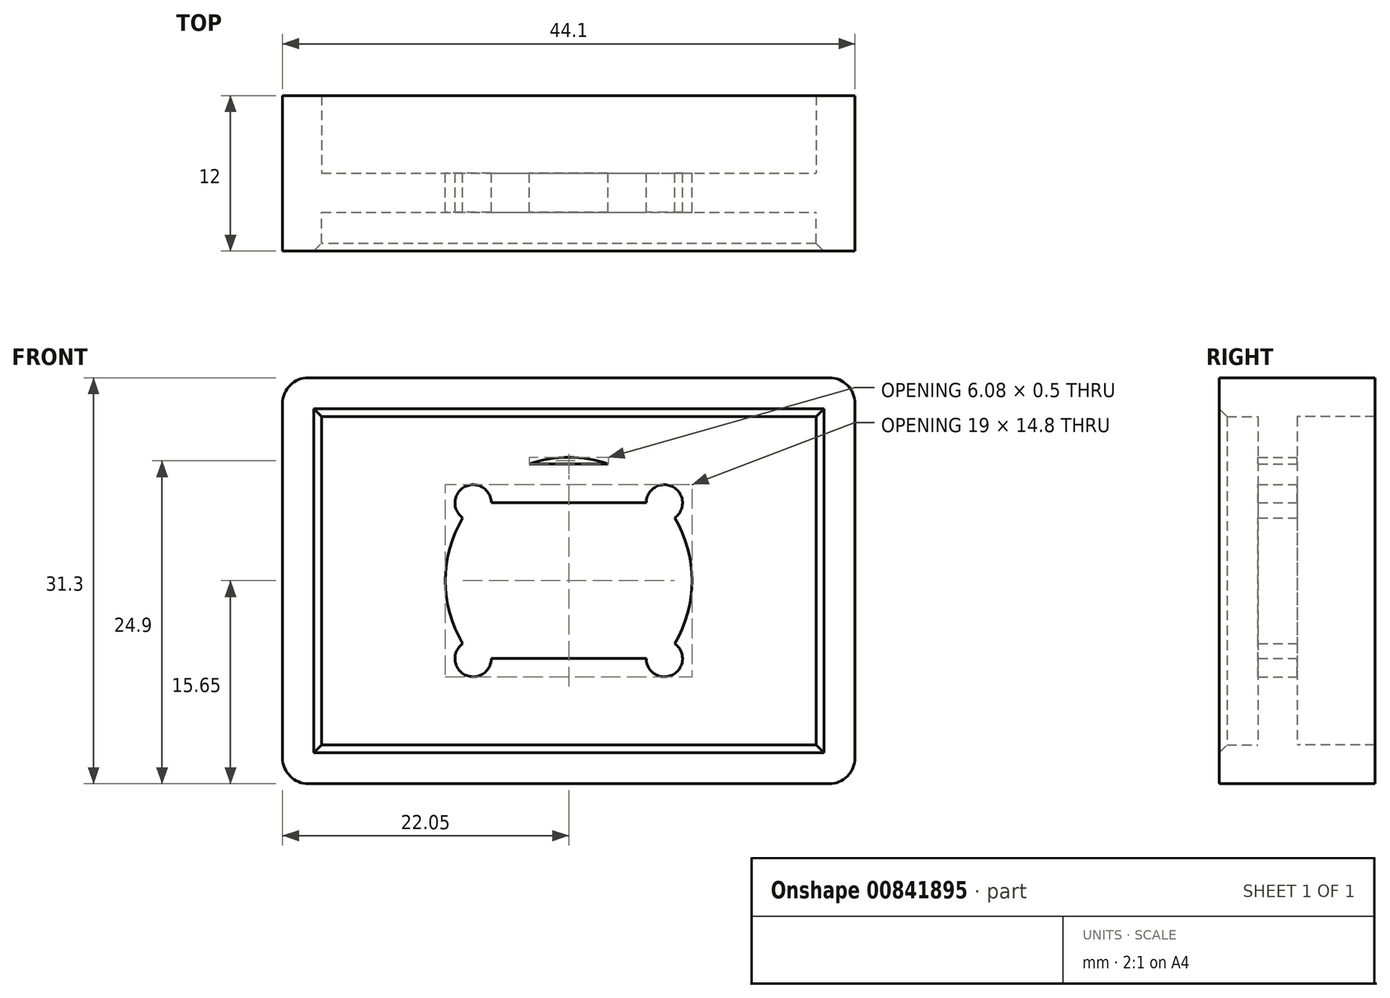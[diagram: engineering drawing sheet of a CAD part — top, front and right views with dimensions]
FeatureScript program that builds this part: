
annotation { "Feature Type Name" : "Feature", "Feature Type Description" : "" }
export const myFeature = defineFeature(function(context is Context, id is Id, definition is map)
    precondition{}
    {
        {
            var Q0;
            Q0=qCreatedBy(makeId("Front.planeOp"),FACE);
            var sketch = newSketch(context, id + "F0", { "sketchPlane" : qUnion([Q0])});
            skLineSegment(sketch, "E0.bottom", {"start": v(-19.05, 12.65) * mm, "end": v(19.05, 12.65) * mm});
            skLineSegment(sketch, "E0.top", {"start": v(-19.05, -12.65) * mm, "end": v(19.05, -12.65) * mm});
            skLineSegment(sketch, "E0.left", {"start": v(-19.05, 12.65) * mm, "end": v(-19.05, -12.65) * mm});
            skLineSegment(sketch, "E0.right", {"start": v(19.05, 12.65) * mm, "end": v(19.05, -12.65) * mm});
            skPoint(sketch, "E0.middle", {"position": v(0, 0) * mm});
            skLineSegment(sketch, "E1.bottom", {"start": v(-22.05, 15.65) * mm, "end": v(22.05, 15.65) * mm});
            skLineSegment(sketch, "E1.top", {"start": v(-22.05, -15.65) * mm, "end": v(22.05, -15.65) * mm});
            skLineSegment(sketch, "E1.left", {"start": v(-22.05, 15.65) * mm, "end": v(-22.05, -15.65) * mm});
            skLineSegment(sketch, "E1.right", {"start": v(22.05, 15.65) * mm, "end": v(22.05, -15.65) * mm});
            skCircle(sketch, "E2", {"center": v(0, 0) * mm, "radius": 9.5 * mm});
            skLineSegment(sketch, "E3.bottom", {"start": v(-9.5, 6) * mm, "end": v(9.5, 6) * mm});
            skLineSegment(sketch, "E3.top", {"start": v(-9.5, -6) * mm, "end": v(9.5, -6) * mm});
            skLineSegment(sketch, "E3.left", {"start": v(-9.5, 6) * mm, "end": v(-9.5, -6) * mm});
            skLineSegment(sketch, "E3.right", {"start": v(9.5, 6) * mm, "end": v(9.5, -6) * mm});
            skCircle(sketch, "E4", {"center": v(0, 0) * mm, "radius": 12.5 * mm});
            skLineSegment(sketch, "E5.bottom", {"start": v(-12.5, 9) * mm, "end": v(12.5, 9) * mm});
            skLineSegment(sketch, "E5.top", {"start": v(-12.5, -9) * mm, "end": v(12.5, -9) * mm});
            skLineSegment(sketch, "E5.left", {"start": v(-12.5, 9) * mm, "end": v(-12.5, -9) * mm});
            skLineSegment(sketch, "E5.right", {"start": v(12.5, 9) * mm, "end": v(12.5, -9) * mm});
            skLineSegment(sketch, "E6.bottom", {"start": v(-7.37, 6) * mm, "end": v(7.37, 6) * mm});
            skLineSegment(sketch, "E6.top", {"start": v(-7.37, -6) * mm, "end": v(7.37, -6) * mm});
            skLineSegment(sketch, "E6.left", {"start": v(-7.37, 6) * mm, "end": v(-7.37, -6) * mm});
            skLineSegment(sketch, "E6.right", {"start": v(7.37, 6) * mm, "end": v(7.37, -6) * mm});
            skCircle(sketch, "E7", {"center": v(-7.37, 6) * mm, "radius": 1.4 * mm});
            skCircle(sketch, "E8", {"center": v(7.37, 6) * mm, "radius": 1.4 * mm});
            skCircle(sketch, "E9", {"center": v(7.37, -6) * mm, "radius": 1.4 * mm});
            skCircle(sketch, "E10", {"center": v(-7.37, -6) * mm, "radius": 1.4 * mm});
            skSolve(sketch);
        }
        {
            var Q0;
            {var subQ0=sQuery(id+"F0.wireOp",EDGE,"diyo5Ijy-Unrl-Ix7s-xjxT-a2Idyrmd7R7O");var subQ1=sQuery(id+"F0.wireOp",EDGE,"E4");var subQ2=makeQuery(id+"F0.imprint","INTERSECT",VERTEX,{"disambiguationData":[OD(0.0)],"derivedFrom":[subQ1,subQ0]});Q0=makeQuery(id+"F0.imprint","IMPRINT",FACE,{"disambiguationData":[TD([[makeQuery(id+"F0.imprint","IMPRINT",EDGE,{"disambiguationData":[TD([[subQ2,-1.0]])],"derivedFrom":subQ1}),1.0]])]});}
            var Q1;
            {var subQ0=sQuery(id+"F0.wireOp",EDGE,"5QQwORZ6-yYhv-RJ5g-prPR-Qrd3KqkXHQQd");var subQ1=sQuery(id+"F0.wireOp",EDGE,"E4");var subQ2=makeQuery(id+"F0.imprint","INTERSECT",VERTEX,{"disambiguationData":[OD(0.0)],"derivedFrom":[subQ1,subQ0]});Q1=makeQuery(id+"F0.imprint","IMPRINT",FACE,{"disambiguationData":[TD([[makeQuery(id+"F0.imprint","IMPRINT",EDGE,{"disambiguationData":[TD([[subQ2,-1.0]])],"derivedFrom":subQ1}),1.0]])]});}
            var Q2;
            Q2=makeQuery(id+"F0.imprint","IMPRINT",FACE,{"disambiguationData":[TD([[makeQuery(id+"F0.imprint","IMPRINT",EDGE,{"derivedFrom":sQuery(id+"F0.wireOp",EDGE,"E0.bottom")}),-1.0]])]});
            var Q3;
            {var subQ0=sQuery(id+"F0.wireOp",EDGE,"E5.bottom");var subQ1=sQuery(id+"F0.wireOp",EDGE,"E2");var subQ2=makeQuery(id+"F0.imprint","INTERSECT",VERTEX,{"disambiguationData":[OD(0.0)],"derivedFrom":[subQ1,subQ0]});Q3=makeQuery(id+"F0.imprint","IMPRINT",FACE,{"disambiguationData":[TD([[makeQuery(id+"F0.imprint","IMPRINT",EDGE,{"disambiguationData":[TD([[subQ2,-1.0]])],"derivedFrom":subQ1}),-1.0]])]});}
            var Q4;
            {var subQ0=sQuery(id+"F0.wireOp",EDGE,"RQsxDqyy-hhwE-D28E-GqSd-PO1LcPHCWcnN");var subQ1=sQuery(id+"F0.wireOp",EDGE,"E4");var subQ2=makeQuery(id+"F0.imprint","INTERSECT",VERTEX,{"disambiguationData":[OD(0.0)],"derivedFrom":[subQ1,subQ0]});Q4=makeQuery(id+"F0.imprint","IMPRINT",FACE,{"disambiguationData":[TD([[makeQuery(id+"F0.imprint","IMPRINT",EDGE,{"disambiguationData":[TD([[subQ2,-1.0]])],"derivedFrom":subQ1}),-1.0]])]});}
            var Q5;
            {var subQ0=sQuery(id+"F0.wireOp",EDGE,"E5.right");var subQ1=sQuery(id+"F0.wireOp",EDGE,"E4");var subQ2=makeQuery(id+"F0.imprint","INTERSECT",VERTEX,{"derivedFrom":[subQ1,subQ0]});Q5=makeQuery(id+"F0.imprint","IMPRINT",FACE,{"disambiguationData":[TD([[makeQuery(id+"F0.imprint","IMPRINT",EDGE,{"disambiguationData":[TD([[subQ2,1.0]])],"derivedFrom":subQ1}),-1.0]])]});}
            var Q6;
            {var subQ0=sQuery(id+"F0.wireOp",EDGE,"E5.top");var subQ1=sQuery(id+"F0.wireOp",EDGE,"E2");var subQ5=makeQuery(id+"F0.imprint","INTERSECT",VERTEX,{"disambiguationData":[OD(0.0)],"derivedFrom":[subQ1,subQ0]});Q6=makeQuery(id+"F0.imprint","IMPRINT",FACE,{"disambiguationData":[TD([[makeQuery(id+"F0.imprint","IMPRINT",EDGE,{"disambiguationData":[TD([[subQ5,-1.0]])],"derivedFrom":subQ1}),-1.0]])]});}
            var Q7;
            {var subQ0=sQuery(id+"F0.wireOp",EDGE,"E5.left");var subQ1=sQuery(id+"F0.wireOp",EDGE,"E4");var subQ2=makeQuery(id+"F0.imprint","INTERSECT",VERTEX,{"derivedFrom":[subQ1,subQ0]});Q7=makeQuery(id+"F0.imprint","IMPRINT",FACE,{"disambiguationData":[TD([[makeQuery(id+"F0.imprint","IMPRINT",EDGE,{"disambiguationData":[TD([[subQ2,-1.0]])],"derivedFrom":subQ1}),-1.0]])]});}
            var Q8;
            {var subQ0=sQuery(id+"F0.wireOp",EDGE,"E5.bottom");var subQ1=sQuery(id+"F0.wireOp",EDGE,"E2");var subQ2=makeQuery(id+"F0.imprint","INTERSECT",VERTEX,{"disambiguationData":[OD(0.0)],"derivedFrom":[subQ1,subQ0]});Q8=makeQuery(id+"F0.imprint","IMPRINT",FACE,{"disambiguationData":[TD([[makeQuery(id+"F0.imprint","IMPRINT",EDGE,{"disambiguationData":[TD([[subQ2,-1.0]])],"derivedFrom":subQ1}),1.0]])]});}
            var Q9;
            {var subQ0=sQuery(id+"F0.wireOp",EDGE,"E5.top");var subQ1=sQuery(id+"F0.wireOp",EDGE,"E2");var subQ2=makeQuery(id+"F0.imprint","INTERSECT",VERTEX,{"disambiguationData":[OD(0.0)],"derivedFrom":[subQ1,subQ0]});Q9=makeQuery(id+"F0.imprint","IMPRINT",FACE,{"disambiguationData":[TD([[makeQuery(id+"F0.imprint","IMPRINT",EDGE,{"disambiguationData":[TD([[subQ2,-1.0]])],"derivedFrom":subQ1}),1.0]])]});}
            var Q10;
            {var subQ0=sQuery(id+"F0.wireOp",EDGE,"diyo5Ijy-Unrl-Ix7s-xjxT-a2Idyrmd7R7O");var subQ1=sQuery(id+"F0.wireOp",EDGE,"E4");var subQ2=makeQuery(id+"F0.imprint","INTERSECT",VERTEX,{"disambiguationData":[OD(1.0)],"derivedFrom":[subQ1,subQ0]});Q10=makeQuery(id+"F0.imprint","IMPRINT",FACE,{"disambiguationData":[TD([[makeQuery(id+"F0.imprint","IMPRINT",EDGE,{"disambiguationData":[TD([[subQ2,-1.0]])],"derivedFrom":subQ1}),-1.0]])]});}
            var Q11;
            {var subQ0=sQuery(id+"F0.wireOp",EDGE,"E5.bottom");var subQ1=sQuery(id+"F0.wireOp",EDGE,"E2");var subQ2=makeQuery(id+"F0.imprint","INTERSECT",VERTEX,{"disambiguationData":[OD(1.0)],"derivedFrom":[subQ1,subQ0]});Q11=makeQuery(id+"F0.imprint","IMPRINT",FACE,{"disambiguationData":[TD([[makeQuery(id+"F0.imprint","IMPRINT",EDGE,{"disambiguationData":[TD([[subQ2,-1.0]])],"derivedFrom":subQ1}),-1.0]])]});}
            var Q12;
            {var subQ0=sQuery(id+"F0.wireOp",EDGE,"diyo5Ijy-Unrl-Ix7s-xjxT-a2Idyrmd7R7O");var subQ1=sQuery(id+"F0.wireOp",EDGE,"E4");var subQ2=makeQuery(id+"F0.imprint","INTERSECT",VERTEX,{"disambiguationData":[OD(0.0)],"derivedFrom":[subQ1,subQ0]});Q12=makeQuery(id+"F0.imprint","IMPRINT",FACE,{"disambiguationData":[TD([[makeQuery(id+"F0.imprint","IMPRINT",EDGE,{"disambiguationData":[TD([[subQ2,-1.0]])],"derivedFrom":subQ1}),-1.0]])]});}
            var Q13;
            {var subQ0=sQuery(id+"F0.wireOp",EDGE,"RQsxDqyy-hhwE-D28E-GqSd-PO1LcPHCWcnN");var subQ1=sQuery(id+"F0.wireOp",EDGE,"E4");var subQ2=makeQuery(id+"F0.imprint","INTERSECT",VERTEX,{"disambiguationData":[OD(0.0)],"derivedFrom":[subQ1,subQ0]});Q13=makeQuery(id+"F0.imprint","IMPRINT",FACE,{"disambiguationData":[TD([[makeQuery(id+"F0.imprint","IMPRINT",EDGE,{"disambiguationData":[TD([[subQ2,1.0]])],"derivedFrom":subQ1}),-1.0]])]});}
            var Q14;
            {var subQ0=sQuery(id+"F0.wireOp",EDGE,"5QQwORZ6-yYhv-RJ5g-prPR-Qrd3KqkXHQQd");var subQ1=sQuery(id+"F0.wireOp",EDGE,"E4");var subQ2=makeQuery(id+"F0.imprint","INTERSECT",VERTEX,{"disambiguationData":[OD(0.0)],"derivedFrom":[subQ1,subQ0]});Q14=makeQuery(id+"F0.imprint","IMPRINT",FACE,{"disambiguationData":[TD([[makeQuery(id+"F0.imprint","IMPRINT",EDGE,{"disambiguationData":[TD([[subQ2,-1.0]])],"derivedFrom":subQ1}),-1.0]])]});}
            var Q15;
            {var subQ0=sQuery(id+"F0.wireOp",EDGE,"Sn6az9JK-Su7q-VoNe-VHIh-EGGie5zRdxJw");var subQ1=sQuery(id+"F0.wireOp",EDGE,"E4");var subQ2=makeQuery(id+"F0.imprint","INTERSECT",VERTEX,{"disambiguationData":[OD(0.0)],"derivedFrom":[subQ1,subQ0]});Q15=makeQuery(id+"F0.imprint","IMPRINT",FACE,{"disambiguationData":[TD([[makeQuery(id+"F0.imprint","IMPRINT",EDGE,{"disambiguationData":[TD([[subQ2,-1.0]])],"derivedFrom":subQ1}),-1.0]])]});}
            var Q16;
            {var subQ6=sQuery(id+"F0.wireOp",EDGE,"E3.left");var subQ7=makeQuery(id+"F0.imprint","INTERSECT",VERTEX,{"derivedFrom":[sQuery(id+"F0.wireOp",EDGE,"E2"),subQ6]});Q16=makeQuery(id+"F0.imprint","IMPRINT",FACE,{"disambiguationData":[TD([[makeQuery(id+"F0.imprint","IMPRINT",EDGE,{"disambiguationData":[TD([[subQ7,1.0]])],"derivedFrom":subQ6}),-1.0]])]});}
            var Q17;
            {var subQ6=sQuery(id+"F0.wireOp",EDGE,"E3.right");var subQ8=makeQuery(id+"F0.imprint","INTERSECT",VERTEX,{"derivedFrom":[sQuery(id+"F0.wireOp",EDGE,"E2"),subQ6]});Q17=makeQuery(id+"F0.imprint","IMPRINT",FACE,{"disambiguationData":[TD([[makeQuery(id+"F0.imprint","IMPRINT",EDGE,{"disambiguationData":[TD([[subQ8,1.0]])],"derivedFrom":subQ6}),1.0]])]});}
            var Q18;
            {var subQ0=sQuery(id+"F0.wireOp",EDGE,"E5.top");var subQ1=sQuery(id+"F0.wireOp",EDGE,"E2");var subQ2=makeQuery(id+"F0.imprint","INTERSECT",VERTEX,{"disambiguationData":[OD(1.0)],"derivedFrom":[subQ1,subQ0]});Q18=makeQuery(id+"F0.imprint","IMPRINT",FACE,{"disambiguationData":[TD([[makeQuery(id+"F0.imprint","IMPRINT",EDGE,{"disambiguationData":[TD([[subQ2,-1.0]])],"derivedFrom":subQ1}),-1.0]])]});}
            var Q19;
            {var subQ0=sQuery(id+"F0.wireOp",EDGE,"E3.right");var subQ1=sQuery(id+"F0.wireOp",EDGE,"E2");var subQ2=makeQuery(id+"F0.imprint","INTERSECT",VERTEX,{"derivedFrom":[subQ1,subQ0]});Q19=makeQuery(id+"F0.imprint","IMPRINT",FACE,{"disambiguationData":[TD([[makeQuery(id+"F0.imprint","IMPRINT",EDGE,{"disambiguationData":[TD([[subQ2,1.0]])],"derivedFrom":subQ1}),-1.0]])]});}
            var Q20;
            {var subQ0=sQuery(id+"F0.wireOp",EDGE,"E3.left");var subQ1=sQuery(id+"F0.wireOp",EDGE,"E2");var subQ2=makeQuery(id+"F0.imprint","INTERSECT",VERTEX,{"derivedFrom":[subQ1,subQ0]});Q20=makeQuery(id+"F0.imprint","IMPRINT",FACE,{"disambiguationData":[TD([[makeQuery(id+"F0.imprint","IMPRINT",EDGE,{"disambiguationData":[TD([[subQ2,-1.0]])],"derivedFrom":subQ1}),-1.0]])]});}
            var Q21;
            {var subQ0=sQuery(id+"F0.wireOp",EDGE,"E3.left");var subQ1=sQuery(id+"F0.wireOp",EDGE,"E3.bottom");var subQ2=makeQuery(id+"F0.imprint","INTERSECT",VERTEX,{"derivedFrom":[subQ1,subQ0]});Q21=makeQuery(id+"F0.imprint","IMPRINT",FACE,{"disambiguationData":[TD([[makeQuery(id+"F0.imprint","IMPRINT",EDGE,{"disambiguationData":[TD([[subQ2,-1.0]])],"derivedFrom":subQ1}),-1.0]])]});}
            var Q22;
            {var subQ0=sQuery(id+"F0.wireOp",EDGE,"E3.right");var subQ1=sQuery(id+"F0.wireOp",EDGE,"E3.bottom");var subQ2=makeQuery(id+"F0.imprint","INTERSECT",VERTEX,{"derivedFrom":[subQ1,subQ0]});Q22=makeQuery(id+"F0.imprint","IMPRINT",FACE,{"disambiguationData":[TD([[makeQuery(id+"F0.imprint","IMPRINT",EDGE,{"disambiguationData":[TD([[subQ2,1.0]])],"derivedFrom":subQ1}),-1.0]])]});}
            var Q23;
            {var subQ0=sQuery(id+"F0.wireOp",EDGE,"E3.left");var subQ1=sQuery(id+"F0.wireOp",EDGE,"E3.top");var subQ2=makeQuery(id+"F0.imprint","INTERSECT",VERTEX,{"derivedFrom":[subQ1,subQ0]});Q23=makeQuery(id+"F0.imprint","IMPRINT",FACE,{"disambiguationData":[TD([[makeQuery(id+"F0.imprint","IMPRINT",EDGE,{"disambiguationData":[TD([[subQ2,-1.0]])],"derivedFrom":subQ1}),1.0]])]});}
            var Q24;
            {var subQ0=sQuery(id+"F0.wireOp",EDGE,"E3.right");var subQ1=sQuery(id+"F0.wireOp",EDGE,"E3.top");var subQ2=makeQuery(id+"F0.imprint","INTERSECT",VERTEX,{"derivedFrom":[subQ1,subQ0]});Q24=makeQuery(id+"F0.imprint","IMPRINT",FACE,{"disambiguationData":[TD([[makeQuery(id+"F0.imprint","IMPRINT",EDGE,{"disambiguationData":[TD([[subQ2,1.0]])],"derivedFrom":subQ1}),1.0]])]});}
            var Q25;
            {var subQ0=sQuery(id+"F0.wireOp",EDGE,"E7");var subQ1=sQuery(id+"F0.wireOp",EDGE,"E4");var subQ2=makeQuery(id+"F0.imprint","INTERSECT",VERTEX,{"disambiguationData":[OD(1.0)],"derivedFrom":[subQ1,subQ0]});Q25=makeQuery(id+"F0.imprint","IMPRINT",FACE,{"disambiguationData":[TD([[makeQuery(id+"F0.imprint","IMPRINT",EDGE,{"disambiguationData":[TD([[subQ2,-1.0]])],"derivedFrom":subQ1}),-1.0]])]});}
            var Q26;
            {var subQ0=sQuery(id+"F0.wireOp",EDGE,"E8");var subQ1=sQuery(id+"F0.wireOp",EDGE,"E4");var subQ2=makeQuery(id+"F0.imprint","INTERSECT",VERTEX,{"disambiguationData":[OD(0.0)],"derivedFrom":[subQ1,subQ0]});Q26=makeQuery(id+"F0.imprint","IMPRINT",FACE,{"disambiguationData":[TD([[makeQuery(id+"F0.imprint","IMPRINT",EDGE,{"disambiguationData":[TD([[subQ2,1.0]])],"derivedFrom":subQ1}),-1.0]])]});}
            var Q27;
            {var subQ0=sQuery(id+"F0.wireOp",EDGE,"E5.bottom");var subQ1=sQuery(id+"F0.wireOp",EDGE,"E4");var subQ2=makeQuery(id+"F0.imprint","INTERSECT",VERTEX,{"disambiguationData":[OD(1.0)],"derivedFrom":[subQ1,subQ0]});Q27=makeQuery(id+"F0.imprint","IMPRINT",FACE,{"disambiguationData":[TD([[makeQuery(id+"F0.imprint","IMPRINT",EDGE,{"disambiguationData":[TD([[subQ2,-1.0]])],"derivedFrom":subQ1}),-1.0]])]});}
            var Q28;
            {var subQ0=sQuery(id+"F0.wireOp",EDGE,"E5.bottom");var subQ1=sQuery(id+"F0.wireOp",EDGE,"E4");var subQ2=makeQuery(id+"F0.imprint","INTERSECT",VERTEX,{"disambiguationData":[OD(0.0)],"derivedFrom":[subQ1,subQ0]});Q28=makeQuery(id+"F0.imprint","IMPRINT",FACE,{"disambiguationData":[TD([[makeQuery(id+"F0.imprint","IMPRINT",EDGE,{"disambiguationData":[TD([[subQ2,1.0]])],"derivedFrom":subQ1}),-1.0]])]});}
            var Q29;
            {var subQ1=sQuery(id+"F0.wireOp",EDGE,"E2");var subQ8=sQuery(id+"F0.wireOp",EDGE,"E8");var subQ10=makeQuery(id+"F0.imprint","INTERSECT",VERTEX,{"disambiguationData":[OD(1.0)],"derivedFrom":[subQ1,subQ8]});Q29=makeQuery(id+"F0.imprint","IMPRINT",FACE,{"disambiguationData":[TD([[makeQuery(id+"F0.imprint","IMPRINT",EDGE,{"disambiguationData":[TD([[subQ10,-1.0]])],"derivedFrom":subQ1}),1.0]])]});}
            var Q30;
            {var subQ1=sQuery(id+"F0.wireOp",EDGE,"E2");var subQ4=sQuery(id+"F0.wireOp",EDGE,"E10");var subQ10=makeQuery(id+"F0.imprint","INTERSECT",VERTEX,{"disambiguationData":[OD(1.0)],"derivedFrom":[subQ1,subQ4]});Q30=makeQuery(id+"F0.imprint","IMPRINT",FACE,{"disambiguationData":[TD([[makeQuery(id+"F0.imprint","IMPRINT",EDGE,{"disambiguationData":[TD([[subQ10,-1.0]])],"derivedFrom":subQ1}),1.0]])]});}
            extrude(context, id + "F1", {"entities" : qUnion([Q0, Q1, Q2, Q3, Q4, Q5, Q6, Q7, Q8, Q9, Q10, Q11, Q12, Q13, Q14, Q15, Q16, Q17, Q18, Q19, Q20, Q21, Q22, Q23, Q24, Q25, Q26, Q27, Q28, Q29, Q30]), "depth" : 3 * mm, "offsetDistance" : 25 * mm});
        }
        {
            var Q0;
            Q0=makeQuery(id+"F0.imprint","IMPRINT",FACE,{"disambiguationData":[TD([[makeQuery(id+"F0.imprint","IMPRINT",EDGE,{"derivedFrom":sQuery(id+"F0.wireOp",EDGE,"E0.bottom")}),1.0]])]});
            extrude(context, id + "F2", {"entities" : qUnion([Q0]), "operationType" : NewBodyOperationType.ADD, "depth" : 6 * mm, "offsetDistance" : 25 * mm});
        }
        {
            var Q0;
            Q0=makeQuery(id+"F0.imprint","IMPRINT",FACE,{"disambiguationData":[TD([[makeQuery(id+"F0.imprint","IMPRINT",EDGE,{"derivedFrom":sQuery(id+"F0.wireOp",EDGE,"E0.bottom")}),1.0]])]});
            extrude(context, id + "F3", {"entities" : qUnion([Q0]), "operationType" : NewBodyOperationType.ADD, "oppositeDirection" : true, "depth" : 6 * mm, "offsetDistance" : 25 * mm});
        }
        {
            var Q0;
            Q0=makeQuery(id+"F2.opExtrude","CAP_EDGE",EDGE,{"disambiguationData":[OSD([sQuery(id+"F0.wireOp",EDGE,"E0.left")])],"isStart":false});
            var Q1;
            Q1=makeQuery(id+"F2.opExtrude","CAP_EDGE",EDGE,{"disambiguationData":[OSD([sQuery(id+"F0.wireOp",EDGE,"E0.top")])],"isStart":false});
            var Q2;
            Q2=makeQuery(id+"F2.opExtrude","CAP_EDGE",EDGE,{"disambiguationData":[OSD([sQuery(id+"F0.wireOp",EDGE,"E0.bottom")])],"isStart":false});
            var Q3;
            Q3=makeQuery(id+"F2.opExtrude","CAP_EDGE",EDGE,{"disambiguationData":[OSD([sQuery(id+"F0.wireOp",EDGE,"E0.right")])],"isStart":false});
            chamfer(context, id + "F4", {"entities" : qUnion([Q0, Q1, Q2, Q3]), "width" : 0.6 * mm, "tangentPropagation" : true});
        }
        {
            var Q0;
            {var subQ0=sQuery(id+"F0.wireOp",EDGE,"E1.right");var subQ1=sQuery(id+"F0.wireOp",EDGE,"E1.bottom");Q0=makeQuery(id+"F3.boolean.opBoolean","MERGE",EDGE,{"derivedFrom":[makeQuery(id+"F2.opExtrude","SWEPT_EDGE",EDGE,{"disambiguationData":[OSD([subQ1,subQ0])]}),makeQuery(id+"F3.opExtrude","SWEPT_EDGE",EDGE,{"disambiguationData":[OSD([subQ1,subQ0])]})]});}
            var Q1;
            {var subQ0=sQuery(id+"F0.wireOp",EDGE,"E1.right");var subQ1=sQuery(id+"F0.wireOp",EDGE,"E1.top");Q1=makeQuery(id+"F3.boolean.opBoolean","MERGE",EDGE,{"derivedFrom":[makeQuery(id+"F2.opExtrude","SWEPT_EDGE",EDGE,{"disambiguationData":[OSD([subQ1,subQ0])]}),makeQuery(id+"F3.opExtrude","SWEPT_EDGE",EDGE,{"disambiguationData":[OSD([subQ1,subQ0])]})]});}
            var Q2;
            {var subQ0=sQuery(id+"F0.wireOp",EDGE,"E1.left");var subQ1=sQuery(id+"F0.wireOp",EDGE,"E1.top");Q2=makeQuery(id+"F3.boolean.opBoolean","MERGE",EDGE,{"derivedFrom":[makeQuery(id+"F2.opExtrude","SWEPT_EDGE",EDGE,{"disambiguationData":[OSD([subQ1,subQ0])]}),makeQuery(id+"F3.opExtrude","SWEPT_EDGE",EDGE,{"disambiguationData":[OSD([subQ1,subQ0])]})]});}
            var Q3;
            {var subQ0=sQuery(id+"F0.wireOp",EDGE,"E1.left");var subQ1=sQuery(id+"F0.wireOp",EDGE,"E1.bottom");Q3=makeQuery(id+"F3.boolean.opBoolean","MERGE",EDGE,{"derivedFrom":[makeQuery(id+"F2.opExtrude","SWEPT_EDGE",EDGE,{"disambiguationData":[OSD([subQ1,subQ0])]}),makeQuery(id+"F3.opExtrude","SWEPT_EDGE",EDGE,{"disambiguationData":[OSD([subQ1,subQ0])]})]});}
            fillet(context, id + "F5", {"entities" : qUnion([Q0, Q1, Q2, Q3]), "radius" : 2 * mm, "tangentPropagation" : true, "allowEdgeOverflow" : false});
        }
    });
